# Revit family: Domotics-DomesticRanges-GEWISS-SYSTEM_COMMAND-ONE-WAY_SWITCH_HEAVY_DUTY
name_source: partatom
category: Apparecchi elettrici
revit_build: Autodesk Revit 2016 (Build: 20161004_0715(x64)
units: mm (PartAtom-declared; Revit-internal decimal feet)

## family parameters
Condiviso = Sì
Host = Superficie
Mantenere orientamento annotazione = Sì
Numero OmniClass = 23.80.50.11.14
Punto di calcolo locali = Sì
Quota connettore circolare = Usa diametro
Taglio con vuoti quando caricato = No
Tipo di parte = Normale
Titolo OmniClass = Switches

## types (2) — shared parameters
Button key = Neutral
Carico apparente = 0 VA
Catalogue = DOMOTICS
Catalogue Range = SYSTEM - DOMESTIC RANGE
Description. = One-way switch (2P - 25 A)
Description: = 25A
Electrocod = 0130
IDF = 703c0208-0ae5-45ba-af99-f43cb316ca8c
IDT = ed97927d-75f9-4dd6-b9f1-08caf59d740d
Immagine tipo = GW21585.jpg
Larghezza pulsante = 23 mm  [stored 0.0754593 ft]
N. poli = 1
No. SYSTEM modules = 1
Produttore = GEWISS S.p.A.
Prospetto di default = 1219 mm
SEO = 1 way switch
Simbolo_ = SIMBOLO INTERRUTTORI : INT2P
Technical sheet = https://www.gewiss.com
Tipo_ = SYSTEM INT HD_BASE : GW21585 - Nero - Interruttore 2P 25A
Type = General
Type of use: = Heavy duty
URL = https://www.gewiss.com
Version file RFA = 19.4
Volt = 230 V
Voltage = 250 V ac
Voltage: = 250 V ac

## per-type parameters (varying)
| type | Colour | Descrizione | EAN code | Modello |
| GW20585 - Switch-2P 25a white | White | SWITCH-2P 25A SY/WT | 8011564190528 | GW20585 |
| GW21585 - Switch-2P 25a black | Black | SWITCH-2P 25A SY/BK | 8011564190535 | GW21585 |

note: [stored X ft] marks values corroborated as IEEE doubles in the binary element streams (Revit-internal decimal feet)

## geometry (parser evidence)
native form markers: Sweep x2
no freeform markers — native parametric forms only
